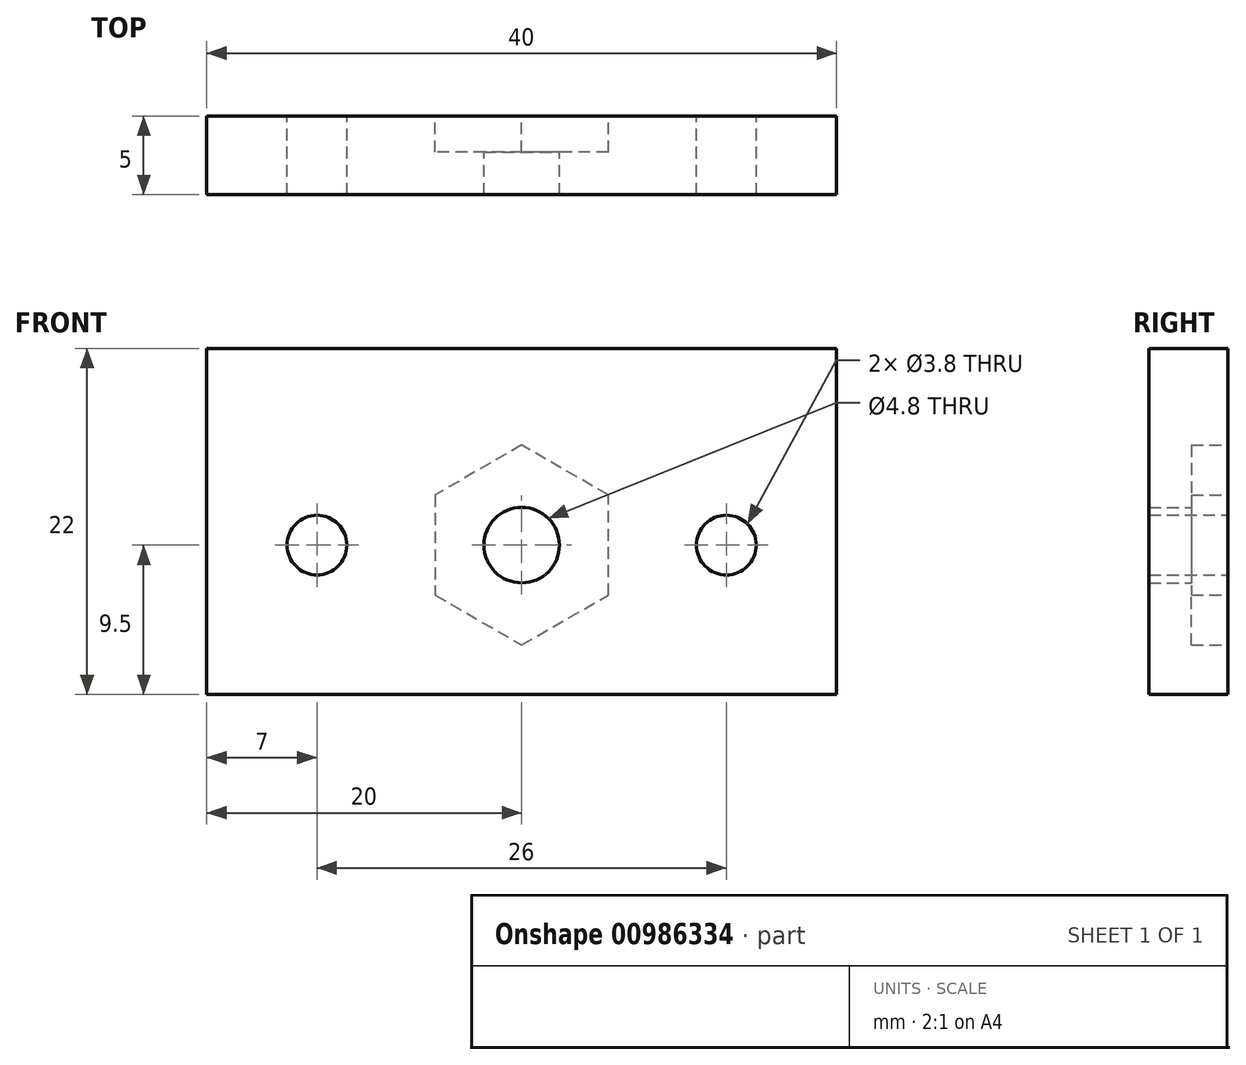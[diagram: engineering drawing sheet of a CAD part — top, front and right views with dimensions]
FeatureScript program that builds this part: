
annotation { "Feature Type Name" : "Feature", "Feature Type Description" : "" }
export const myFeature = defineFeature(function(context is Context, id is Id, definition is map)
    precondition{}
    {
        {
            var Q0;
            Q0=qCreatedBy(makeId("Front.planeOp"),FACE);
            var sketch = newSketch(context, id + "F0", { "sketchPlane" : qUnion([Q0])});
            skLineSegment(sketch, "E0.bottom", {"start": v(0, 0) * mm, "end": v(40, 0) * mm});
            skLineSegment(sketch, "E0.top", {"start": v(0, 22) * mm, "end": v(40, 22) * mm});
            skLineSegment(sketch, "E0.left", {"start": v(0, 0) * mm, "end": v(0, 22) * mm});
            skLineSegment(sketch, "E0.right", {"start": v(40, 0) * mm, "end": v(40, 22) * mm});
            skPoint(sketch, "E1.endSnap0", {"position": v(20, 0) * mm});
            skCircle(sketch, "E2", {"center": v(20, 9.5) * mm, "radius": 2.4 * mm});
            skCircle(sketch, "E3", {"center": v(7, 9.5) * mm, "radius": 1.9 * mm});
            skCircle(sketch, "E4.MirrorC", {"center": v(33, 9.5) * mm, "radius": 1.9 * mm});
            skPoint(sketch, "E1.start.orphan", {"position": v(20, 22) * mm});
            skPoint(sketch, "E5.trimOffspring.end.orphan", {"position": v(14, 9.5) * mm});
            skPoint(sketch, "E6.start.orphan", {"position": v(0, 9.5) * mm});
            skSolve(sketch);
        }
        {
            var Q0;
            Q0=qSketchRegion(id+"F0",true);
            extrude(context, id + "F1", {"entities" : qUnion([Q0]), "depth" : 5 * mm});
        }
        {
            var Q0;
            Q0=makeQuery(id+"F1.opExtrude","CAP_FACE",FACE,{"disambiguationData":[OSD([sQuery(id+"F0.wireOp",EDGE,"E0.bottom"),sQuery(id+"F0.wireOp",EDGE,"E0.top"),sQuery(id+"F0.wireOp",EDGE,"E0.left"),sQuery(id+"F0.wireOp",EDGE,"E0.right"),sQuery(id+"F0.wireOp",EDGE,"E2"),sQuery(id+"F0.wireOp",EDGE,"E3"),sQuery(id+"F0.wireOp",EDGE,"E4.MirrorC")])],"isStart":true});
            var sketch = newSketch(context, id + "F2", { "sketchPlane" : qUnion([Q0])});
            skCircle(sketch, "E7.cCircle", {"center": v(-20, 9.5) * mm, "radius": 5.5 * mm, "construction": true});
            skLineSegment(sketch, "E7.0", {"start": v(-14.5, 12.68) * mm, "end": v(-14.5, 6.32) * mm});
            skLineSegment(sketch, "E7.1", {"start": v(-14.5, 6.32) * mm, "end": v(-20, 3.15) * mm});
            skLineSegment(sketch, "E7.2", {"start": v(-20, 3.15) * mm, "end": v(-25.5, 6.32) * mm});
            skLineSegment(sketch, "E7.3", {"start": v(-25.5, 6.32) * mm, "end": v(-25.5, 12.68) * mm});
            skLineSegment(sketch, "E7.4", {"start": v(-25.5, 12.68) * mm, "end": v(-20, 15.85) * mm});
            skLineSegment(sketch, "E7.5", {"start": v(-20, 15.85) * mm, "end": v(-14.5, 12.68) * mm});
            skPoint(sketch, "E7.0.midPoint", {"position": v(-14.5, 9.5) * mm});
            skSolve(sketch);
        }
        {
            var Q0;
            Q0=qSketchRegion(id+"F2",true);
            extrude(context, id + "F3", {"entities" : qUnion([Q0]), "operationType" : NewBodyOperationType.REMOVE, "oppositeDirection" : true, "depth" : 2.3 * mm});
        }
    });
